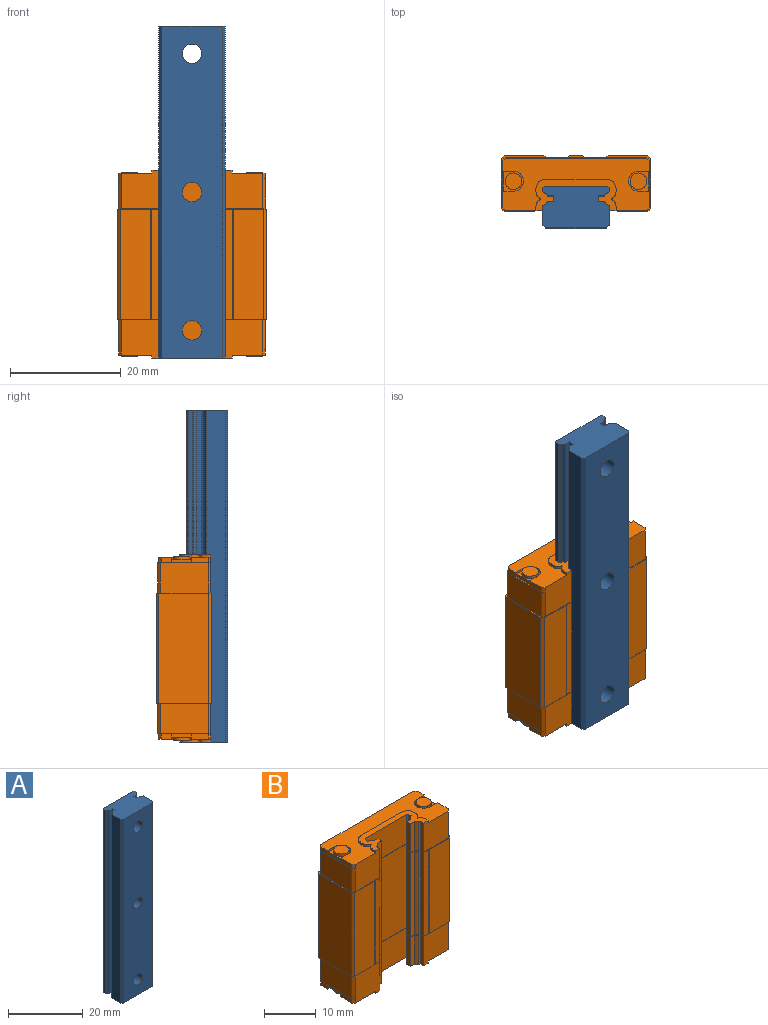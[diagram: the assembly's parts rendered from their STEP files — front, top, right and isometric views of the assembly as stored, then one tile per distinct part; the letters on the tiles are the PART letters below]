
ASSEMBLY  parts=2 mates=1
PART A: 35 faces, bbox 12x7.5x60 mm
  f0: plane 60x0.37mm, normal (0.5,-0.87,0), area 25.5mm2, adj f1,f2,f6,f8
  f1: plane 60x0.74mm, normal (1,0,0), area 44.1mm2, adj f0,f6,f7,f8
  f2: cylinder r=1.32mm len=60mm, axis (0,0,1), area 46.2mm2, adj f0,f6,f8,f34
  f3: plane 60x0.3mm, normal (-0.71,0.71,0), area 25.5mm2, adj f4,f5,f6,f8
  f4: plane 60x0.74mm, normal (-1,0,0), area 44.1mm2, adj f3,f6,f8,f22
  f5: plane 60x11.4mm, normal (0,1,0), area 599.2mm2, adj f3,f6,f7,f8,f9,f12,f15
  f6: plane 12x7.5mm, normal (0,0,1), area 84mm2, adj f0,f1,f2,f3,f4,f5,f7,f18
  f7: plane 60x0.3mm, normal (0.71,0.71,0), area 25.5mm2, adj f1,f5,f6,f8
  f8: plane 12x7.5mm, normal (0,0,-1), area 84mm2, adj f0,f1,f2,f3,f4,f5,f7,f18
  f9: cylinder r=3mm len=6mm, axis (0,1,0), area 84.8mm2, adj f5,f10
  f10: plane 6x6mm, normal (0,1,0), area 18.7mm2, adj f9,f11
  f11: cylinder r=1.75mm len=3.5mm, axis (0,1,0), area 33mm2, adj f10,f18
  f12: cylinder r=3mm len=6mm, axis (0,1,0), area 84.8mm2, adj f5,f13
  f13: plane 6x6mm, normal (0,1,0), area 18.7mm2, adj f12,f14
  f14: cylinder r=1.75mm len=3.5mm, axis (0,1,0), area 33mm2, adj f13,f18
  f15: cylinder r=3mm len=6mm, axis (0,1,0), area 84.8mm2, adj f5,f16
  f16: plane 6x6mm, normal (0,1,0), area 18.7mm2, adj f15,f17
  f17: cylinder r=1.75mm len=3.5mm, axis (0,1,0), area 33mm2, adj f16,f18
  f18: plane 60x11mm, normal (0,-1,0), area 631.1mm2, adj f6,f8,f11,f14,f17,f27,f28
  f19: plane 60x1.11mm, normal (0,-1,0), area 66.7mm2, adj f6,f8,f20,f21
  f20: plane 60x1mm, normal (-1,0,0), area 60mm2, adj f6,f8,f19,f23
  f21: cylinder r=1.32mm len=60mm, axis (0,0,1), area 46.2mm2, adj f6,f8,f19,f22
  f22: plane 60x0.37mm, normal (-0.5,-0.87,0), area 25.5mm2, adj f4,f6,f8,f21
  f23: plane 60x1.11mm, normal (0,1,0), area 66.7mm2, adj f6,f8,f20,f24
  f24: cylinder r=1.32mm len=60mm, axis (0,0,1), area 46.2mm2, adj f6,f8,f23,f25
  f25: plane 60x0.37mm, normal (-0.5,0.87,0), area 25.5mm2, adj f6,f8,f24,f26
  f26: plane 60x3.44mm, normal (-1,0,0), area 206.1mm2, adj f6,f8,f25,f27
  f27: plane 60x0.5mm, normal (-0.71,-0.71,0), area 42.4mm2, adj f6,f8,f18,f26
  f28: plane 60x0.5mm, normal (0.71,-0.71,0), area 42.4mm2, adj f6,f8,f18,f29
  f29: plane 60x3.44mm, normal (1,0,0), area 206.1mm2, adj f6,f8,f28,f30
  f30: plane 60x0.37mm, normal (0.5,0.87,0), area 25.5mm2, adj f6,f8,f29,f31
  f31: cylinder r=1.32mm len=60mm, axis (0,0,1), area 46.2mm2, adj f6,f8,f30,f32
  f32: plane 60x1.11mm, normal (0,1,0), area 66.7mm2, adj f6,f8,f31,f33
  f33: plane 60x1mm, normal (1,0,0), area 60mm2, adj f6,f8,f32,f34
  f34: plane 60x1.11mm, normal (0,-1,0), area 66.7mm2, adj f2,f6,f8,f33
PART B: 242 faces, bbox 27x10x33.9 mm
  f0: cone r=1.23mm half-angle=60deg, axis (0,1,0), area 5.5mm2, adj f193
  f1: plane 6.95x0.74mm, normal (1,0,0), area 5.1mm2, adj f2,f3,f21,f182
  f2: plane 6.95x0.37mm, normal (0.5,0.87,0), area 3mm2, adj f1,f21,f182,f225
  f3: plane 6.95x0.3mm, normal (0.71,-0.71,0), area 2.9mm2, adj f1,f21,f182,f194
  f4: plane 19.9x0.74mm, normal (1,0,0), area 14.6mm2, adj f36,f37,f224,f226
  f5: plane 6.95x0.74mm, normal (1,0,0), area 5.1mm2, adj f9,f117,f118,f135
  f6: plane 6.95x6.8mm, normal (0,-1,0), area 44.4mm2, adj f21,f26,f71,f80,f85,f95,f182,f229
  f7: plane 6.95x6.8mm, normal (0,-1,0), area 44.4mm2, adj f21,f25,f71,f79,f85,f94,f182,f228
  f8: plane 6.95x6.8mm, normal (0,-1,0), area 44.4mm2, adj f9,f16,f32,f57,f66,f116,f135,f232
  f9: plane 14.46x5.63mm, normal (0,0,1), area 31.8mm2, adj f5,f8,f11,f58,f59,f60,f61,f62
  f10: plane 19.9x11.4mm, normal (0,-1,0), area 226.9mm2, adj f36,f37,f197,f226
  f11: plane 6.95x6.8mm, normal (0,-1,0), area 44.4mm2, adj f9,f14,f33,f57,f67,f115,f135,f232
  f12: plane 19.9x0.84mm, normal (1,0,0), area 16.6mm2, adj f36,f37,f214,f241
  f13: plane 19.9x1.28mm, normal (0,-1,0), area 25.4mm2, adj f36,f37,f52,f227
  f14: plane 1x0.5mm, normal (-0.71,-0.71,0), area 0.7mm2, adj f11,f15,f57,f232
  f15: plane 3x1mm, normal (-1,0,0), area 3mm2, adj f14,f17,f57,f232
  f16: plane 1x0.5mm, normal (0.71,-0.71,0), area 0.7mm2, adj f8,f57,f232,f240
  f17: plane 1.95x1mm, normal (0,1,0), area 0.9mm2, adj f15,f18,f57,f99,f100,f232
  f18: cylinder r=1.8mm len=3.6mm, axis (0,0,-1), area 2.3mm2, adj f17,f19,f57,f100
  f19: plane 1.95x1mm, normal (0,-1,0), area 0.9mm2, adj f18,f20,f57,f99,f100,f232
  f20: plane 1.9x1mm, normal (-1,0,0), area 1.9mm2, adj f19,f57,f232,f233
  f21: plane 14.46x5.63mm, normal (0,0,-1), area 31.8mm2, adj f1,f2,f3,f6,f7,f86,f87,f88
  f22: plane 25.6x5.5mm, normal (0,1,0), area 140.8mm2, adj f23,f28,f37,f71
  f23: plane 5.5x0.5mm, normal (0.71,0.71,0), area 3.9mm2, adj f22,f24,f37,f71
  f24: plane 8.6x5.5mm, normal (1,0,0), area 47.3mm2, adj f23,f25,f37,f71
  f25: plane 5.5x0.5mm, normal (0.71,-0.71,0), area 3.9mm2, adj f7,f24,f37,f71,f159,f182
  f26: plane 5.5x0.5mm, normal (-0.71,-0.71,0), area 3.9mm2, adj f6,f27,f37,f71,f181,f182
  f27: plane 8.6x5.5mm, normal (-1,0,0), area 47.3mm2, adj f26,f28,f37,f71
  f28: plane 5.5x0.5mm, normal (-0.71,0.71,0), area 3.9mm2, adj f22,f27,f37,f71
  f29: plane 25.6x5.5mm, normal (0,1,0), area 140.8mm2, adj f30,f35,f36,f232
  f30: plane 5.5x0.5mm, normal (0.71,0.71,0), area 3.9mm2, adj f29,f31,f36,f232
  f31: plane 8.6x5.5mm, normal (1,0,0), area 47.3mm2, adj f30,f32,f36,f232
  f32: plane 5.5x0.5mm, normal (0.71,-0.71,0), area 3.9mm2, adj f8,f31,f36,f135,f136,f232
  f33: plane 5.5x0.5mm, normal (-0.71,-0.71,0), area 3.9mm2, adj f11,f34,f36,f135,f158,f232
  f34: plane 8.6x5.5mm, normal (-1,0,0), area 47.3mm2, adj f33,f35,f36,f232
  f35: plane 5.5x0.5mm, normal (-0.71,0.71,0), area 3.9mm2, adj f29,f34,f36,f232
  f36: plane 27x10mm, normal (0,0,1), area 13.1mm2, adj f4,f10,f12,f13,f29,f30,f31,f32
  f37: plane 27x10mm, normal (0,0,-1), area 13.1mm2, adj f4,f10,f12,f13,f22,f23,f24,f25
  f38: plane 19.9x0.5mm, normal (-0.71,0.71,0), area 14.1mm2, adj f36,f37,f39,f56
  f39: plane 19.9x7.2mm, normal (0,1,0), area 129.1mm2, adj f36,f37,f38,f40,f183,f186
  f40: plane 19.9x0.4mm, normal (0.53,0.85,0), area 9.4mm2, adj f36,f37,f39,f41
  f41: plane 19.9x3.8mm, normal (0,1,0), area 75.6mm2, adj f36,f37,f40,f42
  f42: plane 19.9x0.4mm, normal (-0.53,0.85,0), area 9.4mm2, adj f36,f37,f41,f43
  f43: plane 19.9x2.4mm, normal (0,1,0), area 47.8mm2, adj f36,f37,f42,f44
  f44: plane 19.9x0.4mm, normal (0.53,0.85,0), area 9.4mm2, adj f36,f37,f43,f45
  f45: plane 19.9x3.8mm, normal (0,1,0), area 75.6mm2, adj f36,f37,f44,f46
  f46: plane 19.9x0.4mm, normal (-0.53,0.85,0), area 9.4mm2, adj f36,f37,f45,f47
  f47: plane 19.9x7.2mm, normal (0,1,0), area 129.1mm2, adj f36,f37,f46,f48,f189,f192
  f48: plane 19.9x0.5mm, normal (0.71,0.71,0), area 14.1mm2, adj f36,f37,f47,f49
  f49: plane 19.9x9mm, normal (1,0,0), area 179.1mm2, adj f36,f37,f48,f50
  f50: plane 19.9x0.5mm, normal (0.71,-0.71,0), area 14.1mm2, adj f36,f37,f49,f51
  f51: plane 19.9x5.5mm, normal (0,-1,0), area 109.5mm2, adj f36,f37,f50,f52
  f52: plane 19.9x0.22mm, normal (-0.41,-0.91,0), area 4.9mm2, adj f13,f36,f37,f51
  f53: plane 19.9x0.22mm, normal (0.41,-0.91,0), area 4.9mm2, adj f36,f37,f54,f241
  f54: plane 19.9x5.5mm, normal (0,-1,0), area 109.5mm2, adj f36,f37,f53,f55
  f55: plane 19.9x0.5mm, normal (-0.71,-0.71,0), area 14.1mm2, adj f36,f37,f54,f56
  f56: plane 19.9x9mm, normal (-1,0,0), area 179.1mm2, adj f36,f37,f38,f55
  f57: plane 26.5x9.5mm, normal (0,0,1), area 148.2mm2, adj f8,f11,f14,f15,f16,f17,f18,f19
  f58: plane 0.62x0.5mm, normal (-1,0,0), area 0.3mm2, adj f9,f57,f59,f70
  f59: cylinder r=1.6mm len=1.6mm, axis (0,0,-1), area 1.3mm2, adj f9,f57,f58,f60
  f60: plane 11.26x0.5mm, normal (0,1,0), area 5.6mm2, adj f9,f57,f59,f61
  f61: cylinder r=1.6mm len=1.6mm, axis (0,0,-1), area 1.3mm2, adj f9,f57,f60,f62
  f62: plane 0.62x0.5mm, normal (1,0,0), area 0.3mm2, adj f9,f57,f61,f63
  f63: cylinder r=1.3mm len=1.21mm, axis (0,0,-1), area 0.8mm2, adj f9,f57,f62,f64
  f64: cylinder r=0.1mm len=0.5mm, axis (0,0,-1), area 0.1mm2, adj f9,f57,f63,f65
  f65: cylinder r=1.3mm len=1.21mm, axis (0,0,-1), area 0.8mm2, adj f9,f57,f64,f66
  f66: plane 0.79x0.5mm, normal (1,0,0), area 0.4mm2, adj f8,f9,f57,f65
  f67: plane 0.79x0.5mm, normal (-1,0,0), area 0.4mm2, adj f9,f11,f57,f68
  f68: cylinder r=1.3mm len=1.21mm, axis (0,0,-1), area 0.8mm2, adj f9,f57,f67,f69
  f69: cylinder r=0.1mm len=0.5mm, axis (0,0,-1), area 0.1mm2, adj f9,f57,f68,f70
  f70: cylinder r=1.3mm len=1.21mm, axis (0,0,-1), area 0.8mm2, adj f9,f57,f58,f69
  f71: plane 26.6x9.6mm, normal (0,0,-1), area 5.1mm2, adj f6,f7,f22,f23,f24,f25,f26,f27
  f72: plane 1x0.5mm, normal (-0.71,0.71,0), area 0.7mm2, adj f71,f73,f84,f85
  f73: plane 25.5x1mm, normal (0,1,0), area 25.5mm2, adj f71,f72,f74,f85
  f74: plane 1x0.5mm, normal (0.71,0.71,0), area 0.7mm2, adj f71,f73,f75,f85
  f75: plane 1.9x1mm, normal (1,0,0), area 1.9mm2, adj f71,f74,f76,f85
  f76: plane 1.95x1mm, normal (0,-1,0), area 0.9mm2, adj f71,f75,f85,f105,f106,f230
  f77: plane 1.95x1mm, normal (0,1,0), area 0.9mm2, adj f71,f78,f85,f105,f106,f230
  f78: plane 3x1mm, normal (1,0,0), area 3mm2, adj f71,f77,f79,f85
  f79: plane 1x0.5mm, normal (0.71,-0.71,0), area 0.7mm2, adj f7,f71,f78,f85
  f80: plane 1x0.5mm, normal (-0.71,-0.71,0), area 0.7mm2, adj f6,f71,f81,f85
  f81: plane 3x1mm, normal (-1,0,0), area 3mm2, adj f71,f80,f82,f85
  f82: plane 1.95x1mm, normal (0,1,0), area 0.9mm2, adj f71,f81,f85,f103,f104,f231
  f83: plane 1.95x1mm, normal (0,-1,0), area 0.9mm2, adj f71,f84,f85,f103,f104,f231
  f84: plane 1.9x1mm, normal (-1,0,0), area 1.9mm2, adj f71,f72,f83,f85
  f85: plane 26.5x9.5mm, normal (0,0,-1), area 148.2mm2, adj f6,f7,f72,f73,f74,f75,f76,f77
  f86: plane 0.62x0.5mm, normal (-1,0,0), area 0.3mm2, adj f21,f85,f87,f98
  f87: cylinder r=1.6mm len=1.6mm, axis (0,0,1), area 1.3mm2, adj f21,f85,f86,f88
  f88: plane 11.26x0.5mm, normal (0,1,0), area 5.6mm2, adj f21,f85,f87,f89
  f89: cylinder r=1.6mm len=1.6mm, axis (0,0,1), area 1.3mm2, adj f21,f85,f88,f90
  f90: plane 0.62x0.5mm, normal (1,0,0), area 0.3mm2, adj f21,f85,f89,f91
  f91: cylinder r=1.3mm len=1.21mm, axis (0,0,1), area 0.8mm2, adj f21,f85,f90,f92
  f92: cylinder r=0.1mm len=0.5mm, axis (0,0,1), area 0.1mm2, adj f21,f85,f91,f93
  f93: cylinder r=1.3mm len=1.21mm, axis (0,0,1), area 0.8mm2, adj f21,f85,f92,f94
  f94: plane 0.79x0.5mm, normal (1,0,0), area 0.4mm2, adj f7,f21,f85,f93
  f95: plane 0.79x0.5mm, normal (-1,0,0), area 0.4mm2, adj f6,f21,f85,f96
  f96: cylinder r=1.3mm len=1.21mm, axis (0,0,1), area 0.8mm2, adj f21,f85,f95,f97
  f97: cylinder r=0.1mm len=0.5mm, axis (0,0,1), area 0.1mm2, adj f21,f85,f96,f98
  f98: cylinder r=1.3mm len=1.21mm, axis (0,0,1), area 0.8mm2, adj f21,f85,f86,f97
  f99: plane 3.6x0.6mm, normal (-1,0,0), area 2.2mm2, adj f17,f19,f100,f232
  f100: plane 3.6x3.55mm, normal (0,0,1), area 4.3mm2, adj f17,f18,f19,f99,f108
  f101: plane 3.6x0.6mm, normal (1,0,0), area 2.2mm2, adj f102,f232,f237,f239
  f102: plane 3.6x3.55mm, normal (0,0,1), area 4.3mm2, adj f101,f112,f237,f238,f239
  f103: plane 3.6x0.6mm, normal (-1,0,0), area 2.2mm2, adj f71,f82,f83,f104
  f104: plane 3.6x3.55mm, normal (0,0,-1), area 4.3mm2, adj f82,f83,f103,f109,f231
  f105: plane 3.6x0.6mm, normal (1,0,0), area 2.2mm2, adj f71,f76,f77,f106
  f106: plane 3.6x3.55mm, normal (0,0,-1), area 4.3mm2, adj f76,f77,f105,f113,f230
  f107: plane 3x3mm, normal (0,0,1), area 7.1mm2, adj f108
  f108: cylinder r=1.5mm len=3mm, axis (0,0,1), area 5.7mm2, adj f100,f107
  f109: cylinder r=1.5mm len=3mm, axis (0,0,1), area 5.7mm2, adj f104,f110
  f110: plane 3x3mm, normal (0,0,-1), area 7.1mm2, adj f109
  f111: plane 3x3mm, normal (0,0,1), area 7.1mm2, adj f112
  f112: cylinder r=1.5mm len=3mm, axis (0,0,1), area 5.7mm2, adj f102,f111
  f113: cylinder r=1.5mm len=3mm, axis (0,0,1), area 5.7mm2, adj f106,f114
  f114: plane 3x3mm, normal (0,0,-1), area 7.1mm2, adj f113
  f115: plane 6.95x0.84mm, normal (1,0,0), area 5.8mm2, adj f9,f11,f124,f135
  f116: plane 6.95x0.84mm, normal (-1,0,0), area 5.8mm2, adj f8,f9,f125,f135
  f117: plane 6.95x0.3mm, normal (0.71,-0.71,0), area 2.9mm2, adj f5,f9,f134,f135
  f118: plane 6.95x0.37mm, normal (0.5,0.87,0), area 3mm2, adj f5,f9,f119,f135
  f119: cylinder r=1.32mm len=6.95mm, axis (0,0,1), area 5.3mm2, adj f9,f118,f120,f135
  f120: plane 6.95x1.11mm, normal (0,1,0), area 7.7mm2, adj f9,f119,f121,f135
  f121: plane 6.95x1mm, normal (1,0,0), area 6.9mm2, adj f9,f120,f122,f135
  f122: plane 6.95x1.11mm, normal (0,-1,0), area 7.7mm2, adj f9,f121,f123,f135
  f123: cylinder r=1.32mm len=6.95mm, axis (0,0,1), area 5.3mm2, adj f9,f122,f124,f135
  f124: plane 6.95x0.37mm, normal (0.5,-0.87,0), area 3mm2, adj f9,f115,f123,f135
  f125: plane 6.95x0.37mm, normal (-0.5,-0.87,0), area 3mm2, adj f9,f116,f126,f135
  f126: cylinder r=1.32mm len=6.95mm, axis (0,0,1), area 5.3mm2, adj f9,f125,f127,f135
  f127: plane 6.95x1.11mm, normal (0,-1,0), area 7.7mm2, adj f9,f126,f128,f135
  f128: plane 6.95x1mm, normal (-1,0,0), area 6.9mm2, adj f9,f127,f129,f135
  f129: plane 6.95x1.11mm, normal (0,1,0), area 7.7mm2, adj f9,f128,f130,f135
  f130: cylinder r=1.32mm len=6.95mm, axis (0,0,1), area 5.3mm2, adj f9,f129,f131,f135
  f131: plane 6.95x0.37mm, normal (-0.5,0.87,0), area 3mm2, adj f9,f130,f132,f135
  f132: plane 6.95x0.74mm, normal (-1,0,0), area 5.1mm2, adj f9,f131,f133,f135
  f133: plane 6.95x0.3mm, normal (-0.71,-0.71,0), area 2.9mm2, adj f9,f132,f134,f135
  f134: plane 11.4x6.95mm, normal (0,-1,0), area 79.2mm2, adj f9,f117,f133,f135
  f135: plane 25.7x4.45mm, normal (0,0,-1), area 2mm2, adj f5,f8,f11,f32,f33,f115,f116,f117
  f136: plane 6.8x0.05mm, normal (0,-1,0), area 0.3mm2, adj f32,f36,f135,f137
  f137: plane 0.84x0.05mm, normal (-1,0,0), area 0mm2, adj f36,f135,f136,f138
  f138: plane 0.34x0.18mm, normal (-0.46,-0.89,0), area 0mm2, adj f36,f135,f137,f139
  f139: cylinder r=1.27mm len=0.59mm, axis (0,0,1), area 0mm2, adj f36,f135,f138,f140
  f140: plane 1.09x0.05mm, normal (0,-1,0), area 0.1mm2, adj f36,f135,f139,f141
  f141: plane 0.9x0.05mm, normal (-1,0,0), area 0mm2, adj f36,f135,f140,f142
  f142: plane 1.09x0.05mm, normal (0,1,0), area 0.1mm2, adj f36,f135,f141,f143
  f143: cylinder r=1.27mm len=0.59mm, axis (0,0,1), area 0mm2, adj f36,f135,f142,f144
  f144: plane 0.34x0.18mm, normal (-0.46,0.89,0), area 0mm2, adj f36,f135,f143,f145
  f145: plane 0.84x0.05mm, normal (-1,0,0), area 0mm2, adj f36,f135,f144,f146
  f146: plane 0.3x0.3mm, normal (-0.71,-0.71,0), area 0mm2, adj f36,f135,f145,f147
  f147: plane 11.5x0.05mm, normal (0,-1,0), area 0.6mm2, adj f36,f135,f146,f148
  f148: plane 0.3x0.3mm, normal (0.71,-0.71,0), area 0mm2, adj f36,f135,f147,f149
  f149: plane 0.84x0.05mm, normal (1,0,0), area 0mm2, adj f36,f135,f148,f150
  f150: plane 0.34x0.18mm, normal (0.46,0.89,0), area 0mm2, adj f36,f135,f149,f151
  f151: cylinder r=1.27mm len=0.59mm, axis (0,0,1), area 0mm2, adj f36,f135,f150,f152
  f152: plane 1.09x0.05mm, normal (0,1,0), area 0.1mm2, adj f36,f135,f151,f153
  f153: plane 0.9x0.05mm, normal (1,0,0), area 0mm2, adj f36,f135,f152,f154
  f154: plane 1.09x0.05mm, normal (0,-1,0), area 0.1mm2, adj f36,f135,f153,f155
  f155: cylinder r=1.27mm len=0.59mm, axis (0,0,1), area 0mm2, adj f36,f135,f154,f156
  f156: plane 0.34x0.18mm, normal (0.46,-0.89,0), area 0mm2, adj f36,f135,f155,f157
  f157: plane 0.84x0.05mm, normal (1,0,0), area 0mm2, adj f36,f135,f156,f158
  f158: plane 6.8x0.05mm, normal (0,-1,0), area 0.3mm2, adj f33,f36,f135,f157
  f159: plane 6.8x0.05mm, normal (0,-1,0), area 0.3mm2, adj f25,f37,f160,f182
  f160: plane 0.84x0.05mm, normal (-1,0,0), area 0mm2, adj f37,f159,f161,f182
  f161: plane 0.34x0.18mm, normal (-0.46,-0.89,0), area 0mm2, adj f37,f160,f162,f182
  f162: cylinder r=1.27mm len=0.59mm, axis (0,0,-1), area 0mm2, adj f37,f161,f163,f182
  f163: plane 1.09x0.05mm, normal (0,-1,0), area 0.1mm2, adj f37,f162,f164,f182
  f164: plane 0.9x0.05mm, normal (-1,0,0), area 0mm2, adj f37,f163,f165,f182
  f165: plane 1.09x0.05mm, normal (0,1,0), area 0.1mm2, adj f37,f164,f166,f182
  f166: cylinder r=1.27mm len=0.59mm, axis (0,0,-1), area 0mm2, adj f37,f165,f167,f182
  f167: plane 0.34x0.18mm, normal (-0.46,0.89,0), area 0mm2, adj f37,f166,f168,f182
  f168: plane 0.84x0.05mm, normal (-1,0,0), area 0mm2, adj f37,f167,f169,f182
  f169: plane 0.3x0.3mm, normal (-0.71,-0.71,0), area 0mm2, adj f37,f168,f170,f182
  f170: plane 11.5x0.05mm, normal (0,-1,0), area 0.6mm2, adj f37,f169,f171,f182
  f171: plane 0.3x0.3mm, normal (0.71,-0.71,0), area 0mm2, adj f37,f170,f172,f182
  f172: plane 0.84x0.05mm, normal (1,0,0), area 0mm2, adj f37,f171,f173,f182
  f173: plane 0.34x0.18mm, normal (0.46,0.89,0), area 0mm2, adj f37,f172,f174,f182
  f174: cylinder r=1.27mm len=0.59mm, axis (0,0,-1), area 0mm2, adj f37,f173,f175,f182
  f175: plane 1.09x0.05mm, normal (0,1,0), area 0.1mm2, adj f37,f174,f176,f182
  f176: plane 0.9x0.05mm, normal (1,0,0), area 0mm2, adj f37,f175,f177,f182
  f177: plane 1.09x0.05mm, normal (0,-1,0), area 0.1mm2, adj f37,f176,f178,f182
  f178: cylinder r=1.27mm len=0.59mm, axis (0,0,-1), area 0mm2, adj f37,f177,f179,f182
  f179: plane 0.34x0.18mm, normal (0.46,-0.89,0), area 0mm2, adj f37,f178,f180,f182
  f180: plane 0.84x0.05mm, normal (1,0,0), area 0mm2, adj f37,f179,f181,f182
  f181: plane 6.8x0.05mm, normal (0,-1,0), area 0.3mm2, adj f26,f37,f180,f182
  f182: plane 25.7x4.45mm, normal (0,0,1), area 2mm2, adj f1,f2,f3,f6,f7,f25,f26,f159
  f183: cone r=1.5mm half-angle=45deg, axis (0,1,0), area 3.3mm2, adj f39,f184
  f184: cylinder r=1.23mm len=6.23mm, axis (0,1,0), area 48.1mm2, adj f183,f185
  f185: cone r=1.23mm half-angle=60deg, axis (0,1,0), area 5.5mm2, adj f184
  f186: cone r=1.5mm half-angle=45deg, axis (0,1,0), area 3.3mm2, adj f39,f187
  f187: cylinder r=1.23mm len=6.23mm, axis (0,1,0), area 48.1mm2, adj f186,f188
  f188: cone r=1.23mm half-angle=60deg, axis (0,1,0), area 5.5mm2, adj f187
  f189: cone r=1.5mm half-angle=45deg, axis (0,1,0), area 3.3mm2, adj f47,f190
  f190: cylinder r=1.23mm len=6.23mm, axis (0,1,0), area 48.1mm2, adj f189,f191
  f191: cone r=1.23mm half-angle=60deg, axis (0,1,0), area 5.5mm2, adj f190
  f192: cone r=1.5mm half-angle=45deg, axis (0,1,0), area 3.3mm2, adj f47,f193
  f193: cylinder r=1.23mm len=6.23mm, axis (0,1,0), area 48.1mm2, adj f0,f192
  f194: plane 11.4x6.95mm, normal (0,-1,0), area 79.2mm2, adj f3,f21,f182,f195
  f195: plane 6.95x0.3mm, normal (-0.71,-0.71,0), area 2.9mm2, adj f21,f182,f194,f196
  f196: plane 6.95x0.74mm, normal (-1,0,0), area 5.1mm2, adj f21,f182,f195,f201
  f197: plane 19.9x0.3mm, normal (-0.71,-0.71,0), area 8.4mm2, adj f10,f36,f37,f198
  f198: plane 19.9x0.74mm, normal (-1,0,0), area 14.6mm2, adj f36,f37,f197,f199
  f199: plane 19.9x0.37mm, normal (-0.5,0.87,0), area 8.5mm2, adj f36,f37,f198,f200
  f200: cylinder r=1.32mm len=19.9mm, axis (0,0,1), area 15.3mm2, adj f36,f37,f199,f205
  f201: plane 6.95x0.37mm, normal (-0.5,0.87,0), area 3mm2, adj f21,f182,f196,f202
  f202: cylinder r=1.32mm len=6.95mm, axis (0,0,1), area 5.3mm2, adj f21,f182,f201,f203
  f203: plane 6.95x1.11mm, normal (0,1,0), area 7.7mm2, adj f21,f182,f202,f204
  f204: plane 6.95x1mm, normal (-1,0,0), area 6.9mm2, adj f21,f182,f203,f209
  f205: plane 19.9x1.11mm, normal (0,1,0), area 22.1mm2, adj f36,f37,f200,f206
  f206: plane 19.9x1mm, normal (-1,0,0), area 19.9mm2, adj f36,f37,f205,f207
  f207: plane 19.9x1.11mm, normal (0,-1,0), area 22.1mm2, adj f36,f37,f206,f208
  f208: cylinder r=1.32mm len=19.9mm, axis (0,0,1), area 15.3mm2, adj f36,f37,f207,f213
  f209: plane 6.95x1.11mm, normal (0,-1,0), area 7.7mm2, adj f21,f182,f204,f210
  f210: cylinder r=1.32mm len=6.95mm, axis (0,0,1), area 5.3mm2, adj f21,f182,f209,f211
  f211: plane 6.95x0.37mm, normal (-0.5,-0.87,0), area 3mm2, adj f21,f182,f210,f228
  f212: plane 6.95x0.37mm, normal (0.5,-0.87,0), area 3mm2, adj f21,f182,f217,f229
  f213: plane 19.9x0.37mm, normal (-0.5,-0.87,0), area 8.5mm2, adj f36,f37,f208,f227
  f214: plane 19.9x0.37mm, normal (0.5,-0.87,0), area 8.5mm2, adj f12,f36,f37,f215
  f215: cylinder r=1.32mm len=19.9mm, axis (0,0,1), area 15.3mm2, adj f36,f37,f214,f216
  f216: plane 19.9x1.11mm, normal (0,-1,0), area 22.1mm2, adj f36,f37,f215,f221
  f217: cylinder r=1.32mm len=6.95mm, axis (0,0,1), area 5.3mm2, adj f21,f182,f212,f218
  f218: plane 6.95x1.11mm, normal (0,-1,0), area 7.7mm2, adj f21,f182,f217,f219
  f219: plane 6.95x1mm, normal (1,0,0), area 6.9mm2, adj f21,f182,f218,f220
  f220: plane 6.95x1.11mm, normal (0,1,0), area 7.7mm2, adj f21,f182,f219,f225
  f221: plane 19.9x1mm, normal (1,0,0), area 19.9mm2, adj f36,f37,f216,f222
  f222: plane 19.9x1.11mm, normal (0,1,0), area 22.1mm2, adj f36,f37,f221,f223
  f223: cylinder r=1.32mm len=19.9mm, axis (0,0,1), area 15.3mm2, adj f36,f37,f222,f224
  f224: plane 19.9x0.37mm, normal (0.5,0.87,0), area 8.5mm2, adj f4,f36,f37,f223
  f225: cylinder r=1.32mm len=6.95mm, axis (0,0,1), area 5.3mm2, adj f2,f21,f182,f220
  f226: plane 19.9x0.3mm, normal (0.71,-0.71,0), area 8.4mm2, adj f4,f10,f36,f37
  f227: plane 19.9x0.84mm, normal (-1,0,0), area 16.6mm2, adj f13,f36,f37,f213
  f228: plane 6.95x0.84mm, normal (-1,0,0), area 5.8mm2, adj f7,f21,f182,f211
  f229: plane 6.95x0.84mm, normal (1,0,0), area 5.8mm2, adj f6,f21,f182,f212
  f230: cylinder r=1.8mm len=3.6mm, axis (0,0,1), area 2.3mm2, adj f76,f77,f85,f106
  f231: cylinder r=1.8mm len=3.6mm, axis (0,0,1), area 2.3mm2, adj f82,f83,f85,f104
  f232: plane 26.6x9.6mm, normal (0,0,1), area 5.1mm2, adj f8,f11,f14,f15,f16,f17,f19,f20
  f233: plane 1x0.5mm, normal (-0.71,0.71,0), area 0.7mm2, adj f20,f57,f232,f234
  f234: plane 25.5x1mm, normal (0,1,0), area 25.5mm2, adj f57,f232,f233,f235
  f235: plane 1x0.5mm, normal (0.71,0.71,0), area 0.7mm2, adj f57,f232,f234,f236
  f236: plane 1.9x1mm, normal (1,0,0), area 1.9mm2, adj f57,f232,f235,f237
  f237: plane 1.95x1mm, normal (0,-1,0), area 0.9mm2, adj f57,f101,f102,f232,f236,f238
  f238: cylinder r=1.8mm len=3.6mm, axis (0,0,-1), area 2.3mm2, adj f57,f102,f237,f239
  f239: plane 1.95x1mm, normal (0,1,0), area 0.9mm2, adj f57,f101,f102,f232,f238,f240
  f240: plane 3x1mm, normal (1,0,0), area 3mm2, adj f16,f57,f232,f239
  f241: plane 19.9x1.28mm, normal (0,-1,0), area 25.4mm2, adj f12,f36,f37,f53
PLACE A at identity
PLACE B t=(0,0,-13.05)mm
MATE slider A.f6 <-> B.f9  axis (0,0,1) through (0,7.5,30)mm
